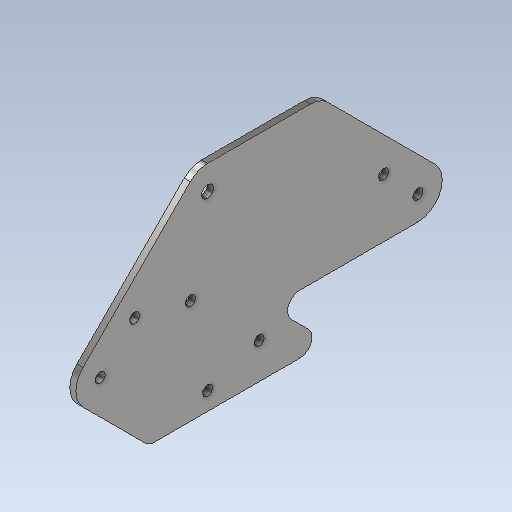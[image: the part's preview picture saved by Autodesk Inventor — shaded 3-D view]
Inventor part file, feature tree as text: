
AUTODESK INVENTOR PART (.ipt)
format: ipt  version: 2023 (Build 270158000, 158)  size: 129,024 bytes
history: native  units: in
note: dims shown in document units (in); Inventor stores cm internally (conversion verified against a paired STEP export)
features: other x3, sketch x1
ambient origin geometry x8: Origin, YZ Plane, XZ Plane, XY Plane, X Axis, Y Axis, Z Axis, Center Point
bodies: Solid1 (feature_tree)
feature tree (4):
  other  "HipPivotPlate.ipt"
  other  "Solid1::HipPivotPlate.ipt"
  other  "TaggingFeature1"
  sketch  "Sketch1"  dims[d0=0.3937in]
